# Revit family: IS_ConnectSpace_E1325_BIM_BE
name_source: partatom
category: Plumbing Fixtures
revit_build: Autodesk Revit 2015 (Build: 20140606_1530(x64)
units: mm (PartAtom-declared; Revit-internal decimal feet)

## types (1)
- E132501 - Connect Space Lavabo Space 600 mm gauche
    Accesoires = www.idealstandard.be
    Afwerking = Wit
    Auteur = Ideal Standard Produktions-GmbH
    Barcode = 5017830447603
    Beschrijvinggarantie = Fabrieksgarantie
    BimObjectNaam = ISI_IdealStandard_Lavabo_Connect_E132501
    Breedte = 0
    BrutoGewicht = 0
    Cost = 0 $
    Default Elevation = 820 mm
    Description = Connect Space Lavabo Space 600 mm gauche
    Diepte = 0 mm  [stored 0 ft]
    Dimensions = 380 x 600 x 172 mm
    DuurEenheid = jaar
    Eigenschappen = Connect Space wastafel in fijne vuurklei met beperkte diepte. 1 kraangat midden doorgestoken. Aflegvlak links of rechts. Te combineren met meubel Space.
    Garantieonderdelen = 10
    Hauteur = 172 mm
    IfcExportAs = IfcSanitaryTerminalType
    IfcExportType = TOILETPANS
    Installatieinstructies = www.idealstandard.be
    Kleur = Wit
    Kleurwc = Wit
    Largeur = 600 mm
    Lengte = 0 mm  [stored 0 ft]
    Longueur = 380 mm  [stored 1.24672 ft]
    Manufacturer = www.idealstandard.be
    Materiaal = fijne vuurklei
    MateriaalWC = fijne vuurklei
    Merk = Ideal Standard
    Model = E132501
    Nettogewicht = 15
    Overloop = 0 mm  [stored 0 ft]
    Productinformatie = www.idealstandard.be
    Telefoonnummer = 0032 2 325 66 00
    Testdruk = 0
    TypeWC = 0
    Typeconnectie = Sanitair
    TypespoelingWC = 0
    URL = www.idealstandard.be
    Uniclass2015Beschrijving = Wash basins, sinks and troughs
    Uniclass2015Referentie = Pr_40_20_96
    Uniclass2015Version = Products v1.1
    Urlproducent = www.idealstandard.be
    Versie = 1
    Vervangingskosten = 0
    Verwachtelevensduur = 25 jaar
    Volumeunits = liter
    Vorm = rechthoekig

note: [stored X ft] marks values corroborated as IEEE doubles in the binary element streams (Revit-internal decimal feet)

## geometry (parser evidence)
native form markers: Blend x4, Sweep x1
no freeform markers — native parametric forms only
